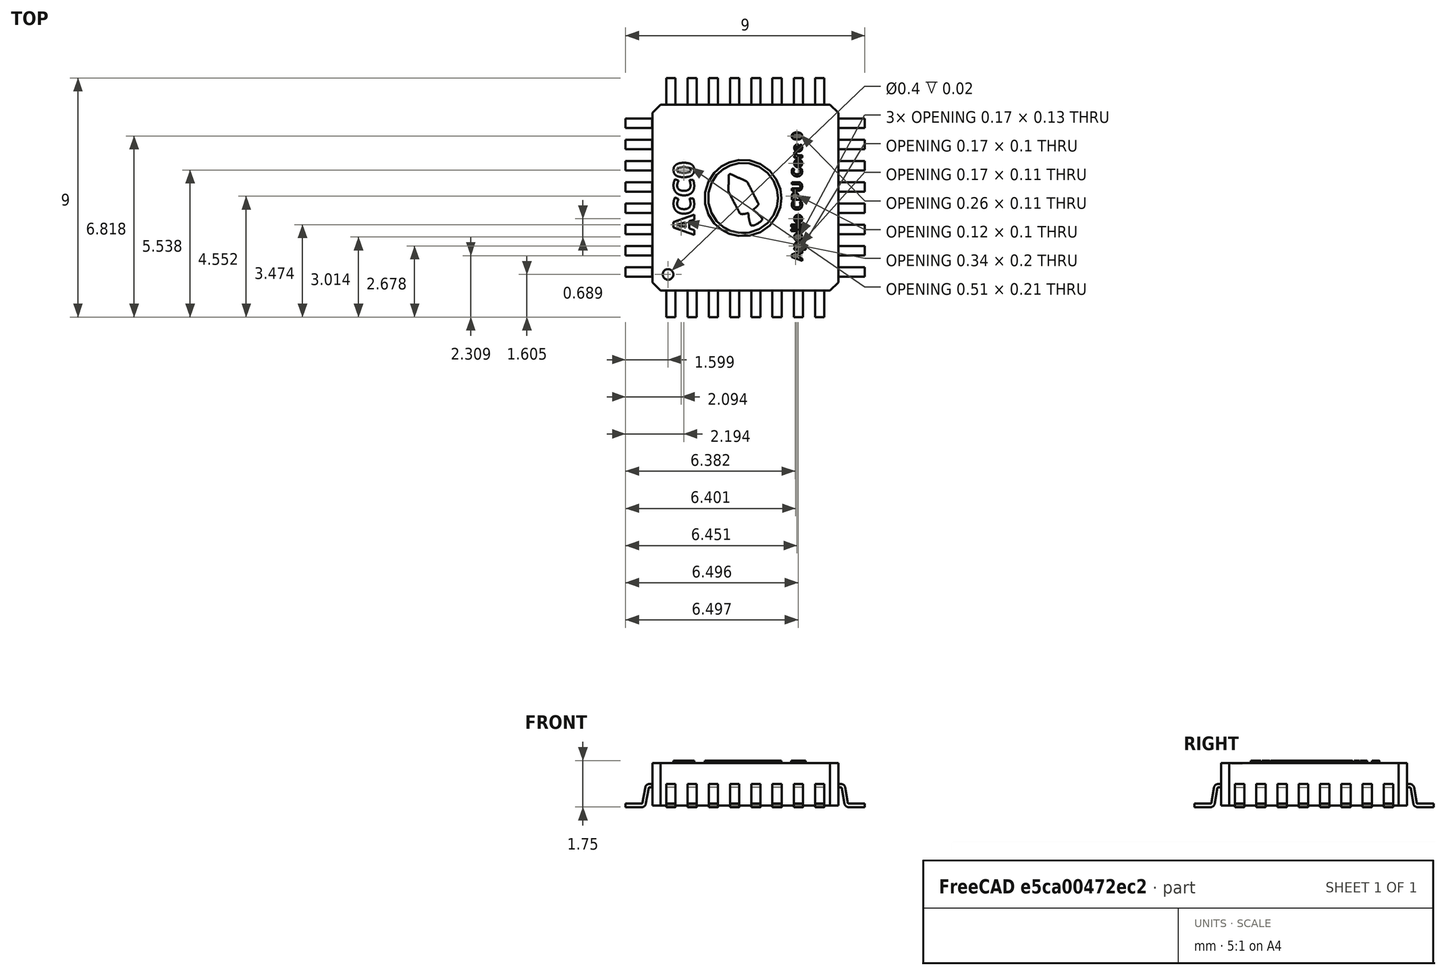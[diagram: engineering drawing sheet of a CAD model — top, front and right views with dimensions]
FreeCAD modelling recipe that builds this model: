
FCSTD DOCUMENT  (FreeCAD 0.16R6703 (Git))
Label: ACC0-chip
License: CC-BY 3.0
LicenseURL: http://creativecommons.org/licenses/by/3.0/
objects: Part::Extrusion×5, Part::Part2DObjectPython×4, Part::FeaturePython×2, Part::Compound×1, Part::Cut×1, Part::MultiFuse×1, App::DocumentObjectGroup×1
note: 14 computed .brp shape members not serialized (recipe doc carries the construction recipe); baked Part::Feature solids carry a one-line shape summary decoded from their .brp

FEATURE [Part::Part2DObjectPython] ShapeString  # Draft 2D object (typed FeaturePython)
  FontFile = <userpath>/develop/fpgawars.github.io/images/src/Open_Sans/OpenSans-Bold.ttf
  Placement = pos=(-9.34532,3.35513,3.3) rot=(0,0,1;0rad)
  Size = 1
  String = ACC0
  Tracking = 0
FEATURE [Part::Extrusion] Extrude001  label="ACC-text"
  Base = -> ShapeString
  Dir = (0,0,0.1)
  Placement = pos=(0.248823,3.2993,0) rot=(0,0,1;1.5708rad)
  Solid = true
FEATURE [Part::Part2DObjectPython] ShapeString001  # Draft 2D object (typed FeaturePython)
  FontFile = <userpath>/develop/fpgawars.github.io/images/src/Open_Sans/OpenSans-Bold.ttf
  Placement = pos=(-9.34532,3.35513,3.3) rot=(0,0,1;0rad)
  Size = 0.5
  String = Apollo CPU Core 0
  Tracking = 0
FEATURE [Part::Extrusion] Extrude002  label="Apollo-cpu-core-Text"
  Base = -> ShapeString001
  Dir = (0,0,0.1)
  Placement = pos=(4.31116,2.32437,0) rot=(0,0,1;1.5708rad)
  Solid = true
FEATURE [Part::Compound] Compound021  label="PQFP-035"
  Placement = pos=(-5.71099,-9.13488,1.7) rot=(0,0,1;0rad)
FEATURE [Part::Extrusion] Extrude  label="logo-orig"
  Dir = (0,0,0.1)
  Placement = pos=(0,0,0) rot=(0,0,1;1.5708rad)
  Solid = true
FEATURE [Part::FeaturePython] Clone  label="logo-ship"  # Draft clone (typed FeaturePython)
  Objects = -> [Extrude]
  Placement = pos=(0.0455738,-4.76068,3.3) rot=(0,0,1;1.5708rad)
  Scale = (0.03,0.03,1)
FEATURE [Part::Part2DObjectPython] Circle  # Draft 2D object (typed FeaturePython)
  FirstAngle = 0
  LastAngle = 0
  MakeFace = true
  Placement = pos=(-0.174267,-5.64836,3.3) rot=(0,0,1;0rad)
  Radius = 1.65
FEATURE [Part::Extrusion] Extrude003  label="Inner-ring"
  Base = -> Circle
  Dir = (0,0,0.3)
  Placement = pos=(0,0,-0.1) rot=(0,0,1;0rad)
  Solid = true
FEATURE [Part::Part2DObjectPython] Circle001  # Draft 2D object (typed FeaturePython)
  FirstAngle = 0
  LastAngle = 0
  MakeFace = true
  Placement = pos=(-0.174267,-5.64836,3.3) rot=(0,0,1;0rad)
  Radius = 1.8
FEATURE [Part::Extrusion] Extrude004  label="Exterior-ring"
  Base = -> Circle001
  Dir = (0,0,0.1)
  Solid = true
FEATURE [Part::Cut] Cut  label="ring"
  Base = -> Extrude004
  Placement = pos=(0.0722774,0.922711,0) rot=(0,0,1;0rad)
  Tool = -> Extrude003
FEATURE [Part::MultiFuse] Fusion  label="logo-union"
  Placement = pos=(-1.14314,0.0422994,0) rot=(0,0,1;0rad)
  Shapes = -> [Clone,Cut]
FEATURE [Part::FeaturePython] Clone001  label="logo"  # Draft clone (typed FeaturePython)
  Objects = -> [Fusion]
  Placement = pos=(-1.4157,-0.869748,0) rot=(0,0,1;0rad)
  Scale = (0.8,0.8,1)
FEATURE [App::DocumentObjectGroup] Group  label="logo-src"
  Group = -> [Extrude,Fusion]
